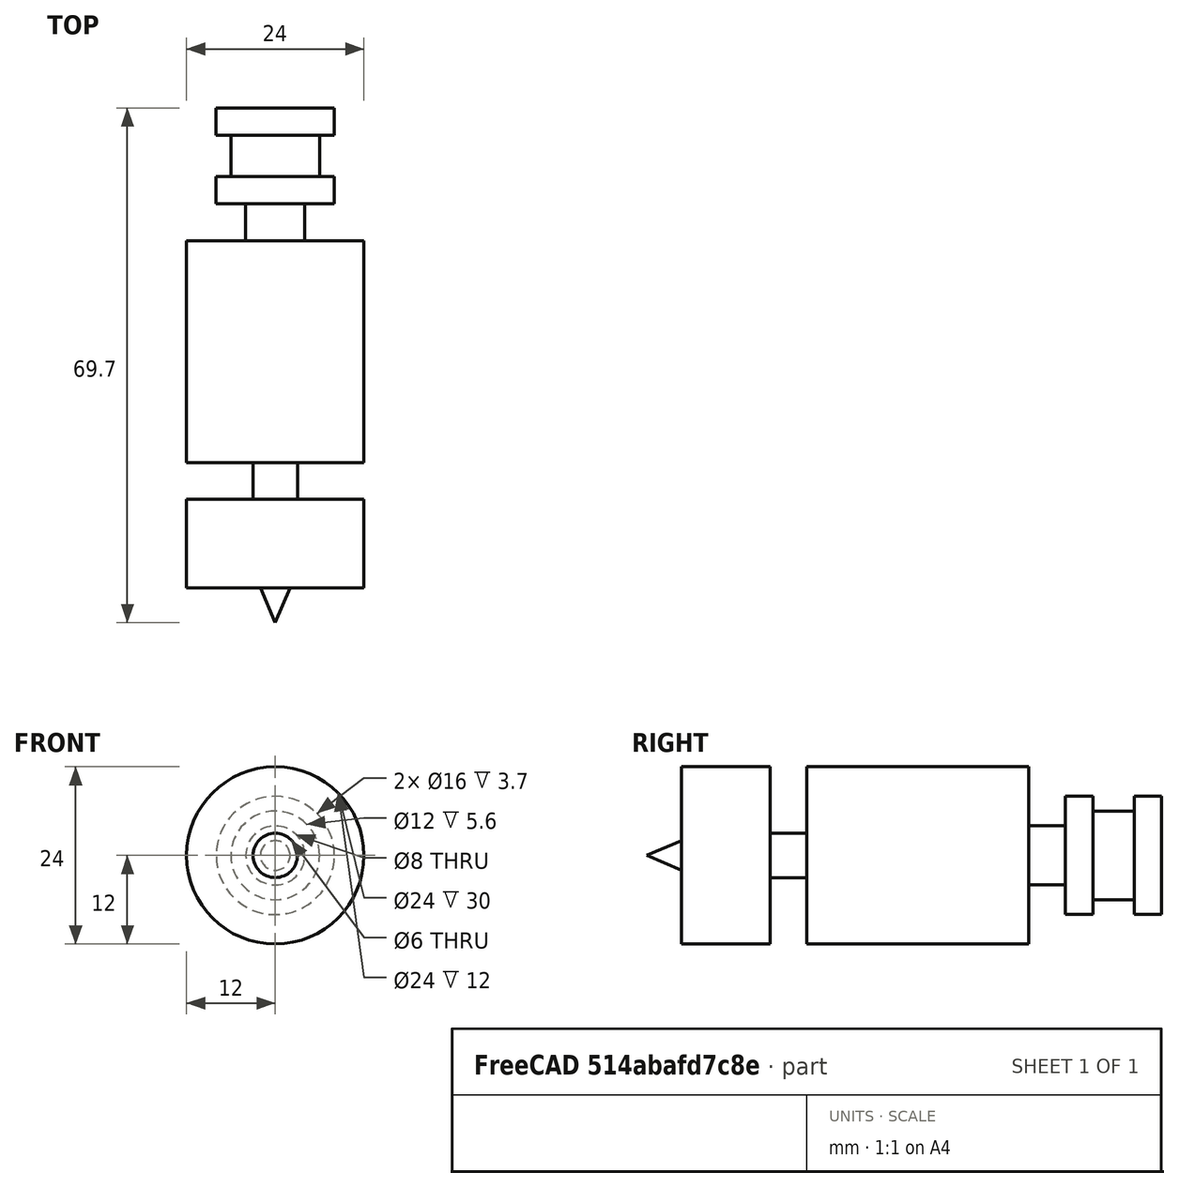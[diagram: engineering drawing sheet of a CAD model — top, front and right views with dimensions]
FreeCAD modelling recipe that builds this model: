
FCSTD DOCUMENT  (FreeCAD 0.16RUnknown)
Label: e3d-v6
License: All rights reserved
LicenseURL: http://en.wikipedia.org/wiki/All_rights_reserved
objects: Sketcher::SketchObject×1, Part::Revolution×1
note: 2 computed .brp shape members not serialized (recipe doc carries the construction recipe); baked Part::Feature solids carry a one-line shape summary decoded from their .brp

FEATURE [Sketcher::SketchObject] Sketch
  sketch-geometry (16):
    g0: LineSegment StartX=0 StartY=34.85 StartZ=0 EndX=-8 EndY=34.85 EndZ=0
    g1: LineSegment StartX=-8 StartY=34.85 StartZ=0 EndX=-8 EndY=31.15 EndZ=0
    g2: LineSegment StartX=-8 StartY=31.15 StartZ=0 EndX=-6 EndY=31.15 EndZ=0
    g3: LineSegment StartX=-6 StartY=31.15 StartZ=0 EndX=-6 EndY=25.55 EndZ=0
    g4: LineSegment StartX=-6 StartY=25.55 StartZ=0 EndX=-8 EndY=25.55 EndZ=0
    g5: LineSegment StartX=-8 StartY=25.55 StartZ=0 EndX=-8 EndY=21.85 EndZ=0
    g6: LineSegment StartX=-8 StartY=21.85 StartZ=0 EndX=-4 EndY=21.85 EndZ=0
    g7: LineSegment StartX=-4 StartY=21.85 StartZ=0 EndX=-4 EndY=16.85 EndZ=0
    g8: LineSegment StartX=-4 StartY=16.85 StartZ=0 EndX=-12 EndY=16.85 EndZ=0
    g9: LineSegment StartX=-12 StartY=16.85 StartZ=0 EndX=-12 EndY=-13.15 EndZ=0
    g10: LineSegment StartX=-12 StartY=-13.15 StartZ=0 EndX=-3 EndY=-13.15 EndZ=0
    g11: LineSegment StartX=-3 StartY=-13.15 StartZ=0 EndX=-3 EndY=-18.15 EndZ=0
    g12: LineSegment StartX=-3 StartY=-18.15 StartZ=0 EndX=-12 EndY=-18.15 EndZ=0
    g13: LineSegment StartX=-12 StartY=-18.15 StartZ=0 EndX=-12 EndY=-30.15 EndZ=0
    g14: LineSegment StartX=-12 StartY=-30.15 StartZ=0 EndX=-2 EndY=-30.15 EndZ=0
    g15: LineSegment StartX=-2 StartY=-30.15 StartZ=0 EndX=0 EndY=-34.85 EndZ=0
  constraints (49):
    c: Horizontal(g0)
    c: Coincident(g0,g1)
    c: Coincident(g1,g2)
    c: Horizontal(g2)
    c: Coincident(g2,g3)
    c: Vertical(g3)
    c: Coincident(g3,g4)
    c: Coincident(g4,g5)
    c: Coincident(g5,g6)
    c: Horizontal(g6)
    c: Coincident(g6,g7)
    c: Coincident(g7,g8)
    c: Horizontal(g8)
    c: Coincident(g8,g9)
    c: Vertical(g9)
    c: Coincident(g9,g10)
    c: Horizontal(g10)
    c: Coincident(g10,g11)
    c: Vertical(g11)
    c: Vertical(g7)
    c: Vertical(g5)
    c: Horizontal(g4)
    c: Vertical(g1)
    c: Coincident(g11,g12)
    c: Horizontal(g12)
    c: Coincident(g12,g13)
    c: Vertical(g13)
    c: Coincident(g13,g14)
    c: Horizontal(g14)
    c: Coincident(g14,g15)
    c: PointOnObject(g15,g-2)
    c: DistanceY(g1,g1) = 3.7
    c: Equal(g5,g1)
    c: DistanceY(g3,g3) = 5.6
    c: DistanceX(g8,g-1) = 12
    c: DistanceX(g0,g0) = 8
    c: Equal(g2,g4)
    c: DistanceY(g15,g0) = 69.7
    c: DistanceX(g0,g-1) = 0
    c: DistanceY(g13,g13) = 12
    c: DistanceX(g12,g9) = 0
    c: DistanceX(g10,g10) = 9
    c: DistanceY(g11,g11) = 5
    c: DistanceY(g7,g7) = 5
    c: DistanceX(g6,g-1) = 4
    c: DistanceY(g9,g9) = 30
    c: DistanceY(g-1,g0) = 34.85
    c: DistanceX(g14,g14) = 10
    c: DistanceX(g2,g-1) = 6
FEATURE [Part::Revolution] Revolve
  Angle = 360
  Axis = (0,1,0)
  Base = (0,0,0)
  Solid = false
  Source = -> Sketch
